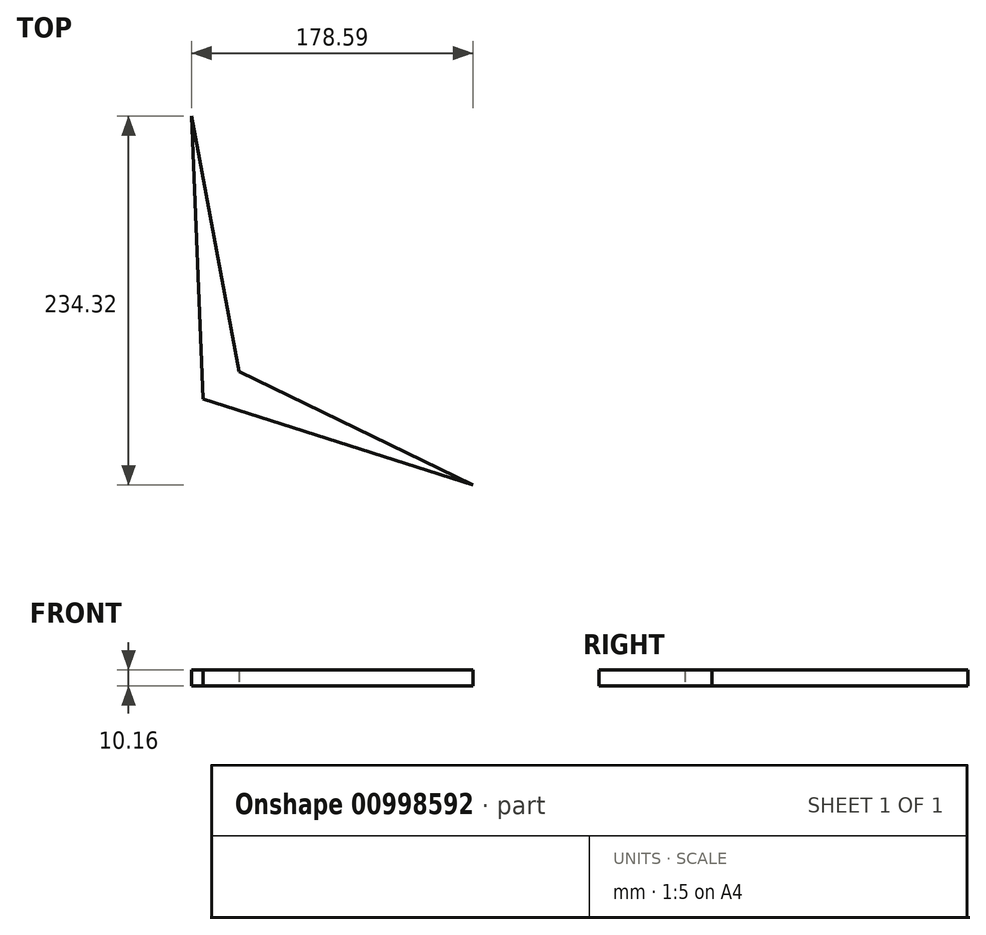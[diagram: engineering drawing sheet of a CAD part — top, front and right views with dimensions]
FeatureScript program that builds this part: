
annotation { "Feature Type Name" : "Feature", "Feature Type Description" : "" }
export const myFeature = defineFeature(function(context is Context, id is Id, definition is map)
    precondition{}
    {
        {
            var Q0;
            Q0=qCreatedBy(makeId("Top.planeOp"),FACE);
            var sketch = newSketch(context, id + "F0", { "sketchPlane" : qUnion([Q0])});
            skLineSegment(sketch, "E0", {"start": v(-146.51, 89.15) * mm, "end": v(-139.25, -90.54) * mm});
            skLineSegment(sketch, "E1", {"start": v(-139.25, -90.54) * mm, "end": v(32.08, -145.17) * mm});
            skLineSegment(sketch, "E2", {"start": v(32.08, -145.17) * mm, "end": v(-116.51, -73.2) * mm});
            skLineSegment(sketch, "E3", {"start": v(-116.51, -73.2) * mm, "end": v(-146.51, 89.15) * mm});
            skSolve(sketch);
        }
        {
            var Q0;
            Q0 = qSketchRegion(id + "F0", true);
            var Q1;
            Q1=makeQuery(id+"F0.imprint","IMPRINT",FACE,{"disambiguationData":[TD([[makeQuery(id+"F0.imprint","IMPRINT",EDGE,{"derivedFrom":sQuery(id+"F0.wireOp",EDGE,"E0")}),1.0]])]});
            extrude(context, id + "F1", {"entities" : qUnion([Q0, Q1]), "depth" : 10.16 * mm, "offsetDistance" : 25.4 * mm});
        }
    });
